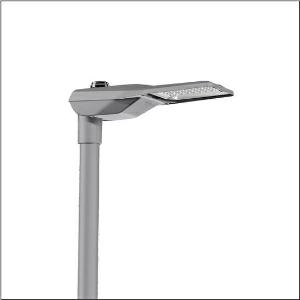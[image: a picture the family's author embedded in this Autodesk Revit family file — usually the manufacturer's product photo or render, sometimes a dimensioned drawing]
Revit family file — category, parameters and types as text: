
# Revit family: streetlight_sl_21_mini___st0_5a_5xe6b47n08jb_72a7
name_source: partatom
category: Lighting Fixtures
units: mm (PartAtom-declared; Revit-internal decimal feet)

## family parameters
Cut with Voids When Loaded = No
Host = Face
Light Source = No
Part Type = Normal
Room Calculation Point = No
Round Connector Dimension = Use Diameter
Shared = No

## types (1)
- --- (1 x LED, 13390 lm, 87.3 W, 4000K)
    Apparent Load = 87 VA
    CIE Flux Codes = 43 76 97 100 100
    Color Rendering = 70
    Color Temperature = 4000K
    Default Elevation = 1800 mm
    Description = Streetlight SL 21 mini, mast luminaire, primary light control with lens, of PMMA, primary optical cover: cover, of toughened safety glass, transparent, light distribution: ST0.5a, light emission: direct distribution, primary light characteristic: asymmetric, installation type: side-entry, LED, 3G 2.5mm², High Power LED, rated luminous flux: 13.390lm, luminous efficacy: 153lm/W, light colour: 740, colour temperature: 4000K, control: overheat protection, pre-setting: linear dimming characteristic, constant luminous flux control, time-dependent luminous flux control, flexible luminous flux parameterisation, mains connection: 230..240V, AC, 50/60Hz, connection cable pre-assembled, cable length: 10,5m, wiring characteristics: H05VV-F, start of lifetime: 87W, end of service life: 90W, reduction: 40W, luminaire housing, of diecast aluminium (EN AC-44300), powder-coated, Siteco® metallic grey (DB 702S), corrosivity category C5 mid according to DIN EN ISO 12944, multi-level sealing system, sealing non-destructively replaceable, inclination adjustable: 0°, 5°, 10°, 15°, length: 628mm, width: 235mm, height: 110mm, spigot size: 42mm (side-entry), protection rating (complete): IP66, insulation class (complete): insulation class I (protective earthing), certification: CE, ENEC, ENEC+, VDE, impact resistance: IK09, permissible operating ambient temperature for outdoor applications: -40..+50°C, standard-compliant lighting for roads and squares, packaging unit: 1 piece

Light Distribution: ST0.5a
    Height = 110 mm
    Lamp = 1 x LED
    Lamp Light Flux = 13390 lm
    Lamp Power = 87.3 W
    Lamp count = 1
    Length = 625 mm
    Luminous efficacy = 153 lm/W
    Manufacturer = Siteco
    ModVariant = No
    Model = 5XE6B47N08JB
    Number of Poles = 1
    OnlyDefault = Yes
    Power Factor = 1
    Product Name = Streetlight SL 21 mini | ST0.5a
    Product group = mast luminaire | pylon top
    ProductGroupID = 6100
    Protection Class = Protection class I
    Protection Degree = IP 66
    RLX_Detail_Level = 1
    RLX_Emergency_Light_Flux = 0 lm
    RLX_Emergency_Type = 0
    RLX_Emergency_Type_DB = No
    RlxData = <blob elided: 103301 chars, md5=2a39258a>
    Socket = socket
    Standby Power = 0 W
    System Light Flux = 13390 lm
    System Power = 87 W
    Type Comments = factory setting: luminous flux: 100 % | dim-lin: 254 | 915 mA
    Type Image = l_1294379.jpg
    URL = http://relux.com
    VarID = @adj_106533
    Voltage = 0 V
    Weight = 0.00 kg
    Width = 234 mm

## geometry (parser evidence)
native form markers: Blend x4, Sweep x10
no freeform markers — native parametric forms only
